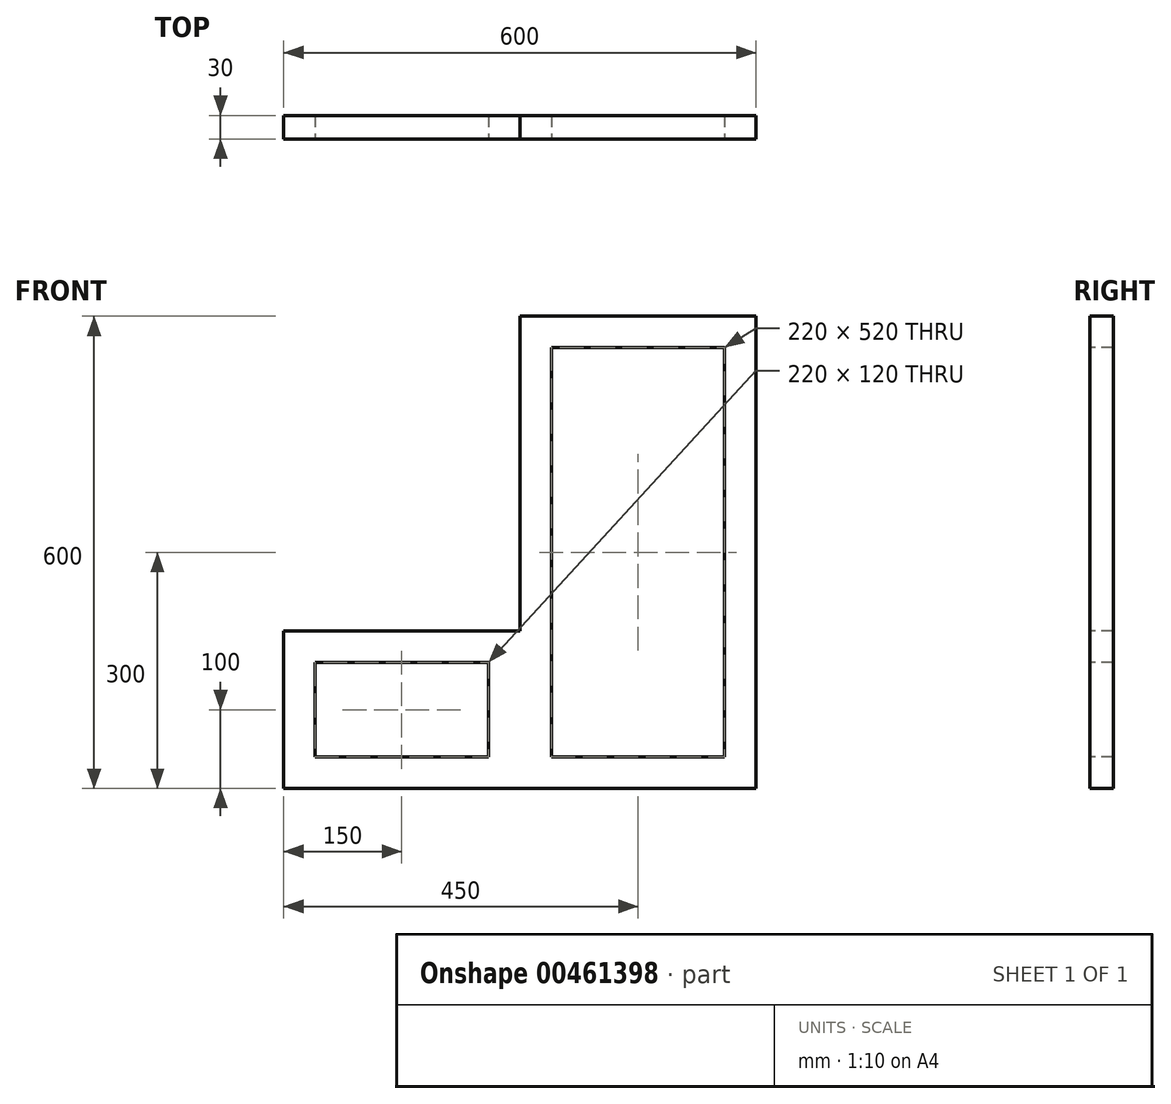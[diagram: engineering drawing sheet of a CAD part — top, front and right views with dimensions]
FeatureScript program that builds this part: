
annotation { "Feature Type Name" : "Feature", "Feature Type Description" : "" }
export const myFeature = defineFeature(function(context is Context, id is Id, definition is map)
    precondition{}
    {
        {
            var Q0;
            Q0=qCreatedBy(makeId("Front.planeOp"),FACE);
            var sketch = newSketch(context, id + "F0", { "sketchPlane" : qUnion([Q0])});
            skLineSegment(sketch, "E0.bottom", {"start": v(0, 0) * mm, "end": v(300, 0) * mm});
            skLineSegment(sketch, "E0.top", {"start": v(0, 600) * mm, "end": v(300, 600) * mm});
            skLineSegment(sketch, "E0.left", {"start": v(0, 0) * mm, "end": v(0, 600) * mm});
            skLineSegment(sketch, "E0.right", {"start": v(300, 0) * mm, "end": v(300, 600) * mm});
            skSolve(sketch);
        }
        {
            var Q0;
            Q0=makeQuery(id+"F0.imprint","IMPRINT",FACE,{"disambiguationData":[TD([[makeQuery(id+"F0.imprint","IMPRINT",EDGE,{"derivedFrom":sQuery(id+"F0.wireOp",EDGE,"E0.bottom")}),1.0]])]});
            extrude(context, id + "F1", {"entities" : qUnion([Q0]), "oppositeDirection" : true, "depth" : 30 * mm});
        }
        {
            var Q0;
            Q0=makeQuery(id+"F1.opExtrude","CAP_FACE",FACE,{"disambiguationData":[OSD([sQuery(id+"F0.wireOp",EDGE,"E0.bottom"),sQuery(id+"F0.wireOp",EDGE,"E0.top"),sQuery(id+"F0.wireOp",EDGE,"E0.left"),sQuery(id+"F0.wireOp",EDGE,"E0.right")])],"isStart":true});
            var sketch = newSketch(context, id + "F2", { "sketchPlane" : qUnion([Q0])});
            skLineSegment(sketch, "E1.bottom", {"start": v(40, 40) * mm, "end": v(260, 40) * mm});
            skLineSegment(sketch, "E1.top", {"start": v(40, 560) * mm, "end": v(260, 560) * mm});
            skLineSegment(sketch, "E1.left", {"start": v(40, 40) * mm, "end": v(40, 560) * mm});
            skLineSegment(sketch, "E1.right", {"start": v(260, 40) * mm, "end": v(260, 560) * mm});
            skSolve(sketch);
        }
        {
            var Q0;
            Q0=makeQuery(id+"F2.imprint","IMPRINT",FACE,{"disambiguationData":[TD([[makeQuery(id+"F2.imprint","IMPRINT",EDGE,{"derivedFrom":sQuery(id+"F2.wireOp",EDGE,"E1.bottom")}),1.0]])]});
            extrude(context, id + "F3", {"entities" : qUnion([Q0]), "operationType" : NewBodyOperationType.REMOVE, "oppositeDirection" : true, "depth" : 35 * mm});
        }
        {
            var Q0;
            Q0=qCreatedBy(makeId("Front.planeOp"),FACE);
            var sketch = newSketch(context, id + "F4", { "sketchPlane" : qUnion([Q0])});
            skLineSegment(sketch, "E2.bottom", {"start": v(0, 0) * mm, "end": v(-300, 0) * mm});
            skLineSegment(sketch, "E2.top", {"start": v(0, 200) * mm, "end": v(-300, 200) * mm});
            skLineSegment(sketch, "E2.left", {"start": v(0, 0) * mm, "end": v(0, 200) * mm});
            skLineSegment(sketch, "E2.right", {"start": v(-300, 0) * mm, "end": v(-300, 200) * mm});
            skSolve(sketch);
        }
        {
            var Q0;
            Q0=makeQuery(id+"F4.imprint","IMPRINT",FACE,{"disambiguationData":[TD([[makeQuery(id+"F4.imprint","IMPRINT",EDGE,{"derivedFrom":sQuery(id+"F4.wireOp",EDGE,"E2.bottom")}),-1.0]])]});
            extrude(context, id + "F5", {"entities" : qUnion([Q0]), "operationType" : NewBodyOperationType.ADD, "oppositeDirection" : true, "depth" : 30 * mm});
        }
        {
            var Q0;
            Q0=makeQuery(id+"F5.boolean.opBoolean","MERGE",FACE,{"derivedFrom":[makeQuery(id+"F1.opExtrude","CAP_FACE",FACE,{"disambiguationData":[OSD([sQuery(id+"F0.wireOp",EDGE,"E0.bottom"),sQuery(id+"F0.wireOp",EDGE,"E0.top"),sQuery(id+"F0.wireOp",EDGE,"E0.left"),sQuery(id+"F0.wireOp",EDGE,"E0.right")])],"isStart":true}),makeQuery(id+"F5.opExtrude","CAP_FACE",FACE,{"disambiguationData":[OSD([sQuery(id+"F4.wireOp",EDGE,"E2.bottom"),sQuery(id+"F4.wireOp",EDGE,"E2.top"),sQuery(id+"F4.wireOp",EDGE,"E2.left"),sQuery(id+"F4.wireOp",EDGE,"E2.right")])],"isStart":true})]});
            var sketch = newSketch(context, id + "F6", { "sketchPlane" : qUnion([Q0])});
            skLineSegment(sketch, "E3.bottom", {"start": v(-260, 160) * mm, "end": v(-40, 160) * mm});
            skLineSegment(sketch, "E3.top", {"start": v(-260, 40) * mm, "end": v(-40, 40) * mm});
            skLineSegment(sketch, "E3.left", {"start": v(-260, 160) * mm, "end": v(-260, 40) * mm});
            skLineSegment(sketch, "E3.right", {"start": v(-40, 160) * mm, "end": v(-40, 40) * mm});
            skSolve(sketch);
        }
        {
            var Q0;
            Q0=makeQuery(id+"F6.imprint","IMPRINT",FACE,{"disambiguationData":[TD([[makeQuery(id+"F6.imprint","IMPRINT",EDGE,{"derivedFrom":sQuery(id+"F6.wireOp",EDGE,"E3.bottom")}),-1.0]])]});
            extrude(context, id + "F7", {"entities" : qUnion([Q0]), "operationType" : NewBodyOperationType.REMOVE, "oppositeDirection" : true, "depth" : 40 * mm});
        }
    });
